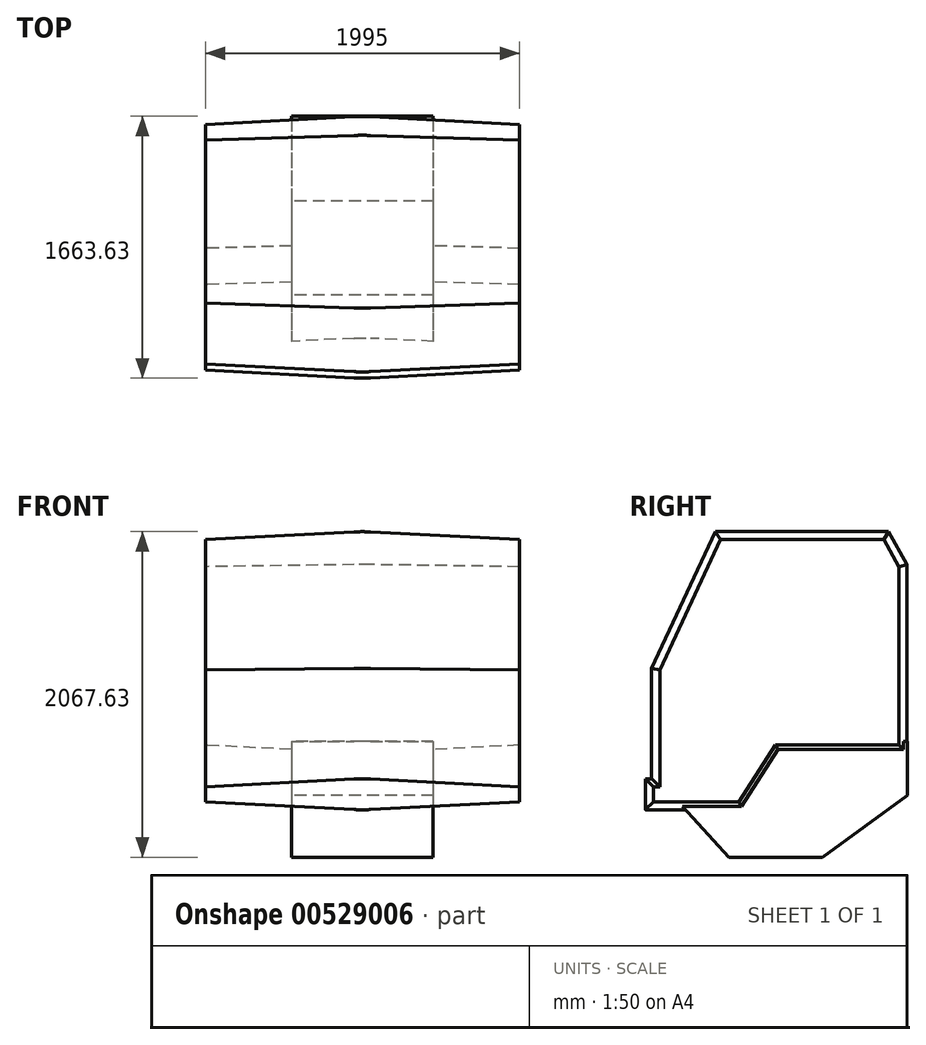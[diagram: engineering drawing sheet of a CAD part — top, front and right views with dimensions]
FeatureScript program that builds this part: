
annotation { "Feature Type Name" : "Feature", "Feature Type Description" : "" }
export const myFeature = defineFeature(function(context is Context, id is Id, definition is map)
    precondition{}
    {
        {
            var Q0;
            Q0=qCreatedBy(makeId("Right.planeOp"),FACE);
            var sketch = newSketch(context, id + "F0", { "sketchPlane" : qUnion([Q0])});
            skLineSegment(sketch, "E0", {"start": v(0, 0) * mm, "end": v(0, 2408.1) * mm, "construction": true});
            skLineSegment(sketch, "E1", {"start": v(540, 660) * mm, "end": v(540, 1859) * mm});
            skLineSegment(sketch, "E2", {"start": v(540, 1859) * mm, "end": v(420, 2069) * mm});
            skLineSegment(sketch, "E3", {"start": v(420, 2069) * mm, "end": v(-679.78, 2069) * mm});
            skLineSegment(sketch, "E4", {"start": v(-679.78, 2069) * mm, "end": v(-1085, 1200) * mm});
            skLineSegment(sketch, "E5", {"start": v(-1085, 1200) * mm, "end": v(-1085, 500) * mm});
            skLineSegment(sketch, "E6", {"start": v(-1085, 500) * mm, "end": v(-1125, 500) * mm});
            skLineSegment(sketch, "E7", {"start": v(-1125, 500) * mm, "end": v(-1125, 300) * mm});
            skLineSegment(sketch, "E8", {"start": v(-1125, 300) * mm, "end": v(-500, 300) * mm});
            skLineSegment(sketch, "E9", {"start": v(-500, 300) * mm, "end": v(-270, 660) * mm});
            skLineSegment(sketch, "E10", {"start": v(-270, 660) * mm, "end": v(540, 660) * mm});
            skLineSegment(sketch, "E11", {"start": v(0, 560) * mm, "end": v(1375.56, 560) * mm, "construction": true});
            skSolve(sketch);
        }
        {
            var Q0;
            Q0=makeQuery(id+"F0.imprint","IMPRINT",FACE,{"disambiguationData":[TD([[makeQuery(id+"F0.imprint","IMPRINT",EDGE,{"derivedFrom":sQuery(id+"F0.wireOp",EDGE,"E1")}),1.0]])]});
            extrude(context, id + "F1", {"entities" : qUnion([Q0]), "endBound" : BoundingType.SYMMETRIC, "depth" : 1995 * mm, "offsetDistance" : 25 * mm, "hasDraft" : true, "draftAngle" : 3 * degree, "draftPullDirection" : true});
        }
        {
            var Q0;
            Q0=qCreatedBy(makeId("Right.planeOp"),FACE);
            var sketch = newSketch(context, id + "F2", { "sketchPlane" : qUnion([Q0])});
            skLineSegment(sketch, "E12.0", {"start": v(-270, 660) * mm, "end": v(540, 660) * mm, "construction": true});
            skLineSegment(sketch, "E13", {"start": v(540, 660) * mm, "end": v(540, 391.7) * mm});
            skLineSegment(sketch, "E14", {"start": v(540, 391.7) * mm, "end": v(0, 0) * mm});
            skLineSegment(sketch, "E15", {"start": v(0, 0) * mm, "end": v(-594.52, 0) * mm});
            skLineSegment(sketch, "E16", {"start": v(-594.52, 735.26) * mm, "end": v(540, 735.26) * mm});
            skLineSegment(sketch, "E17", {"start": v(540, 735.26) * mm, "end": v(540, 660) * mm});
            skLineSegment(sketch, "E18", {"start": v(-594.52, 0) * mm, "end": v(-956.76, 397.83) * mm});
            skLineSegment(sketch, "E19", {"start": v(-956.76, 397.83) * mm, "end": v(-594.52, 735.26) * mm});
            skSolve(sketch);
        }
        {
            var Q0;
            Q0=makeQuery(id+"F2.imprint","IMPRINT",FACE,{"disambiguationData":[TD([[makeQuery(id+"F2.imprint","IMPRINT",EDGE,{"derivedFrom":sQuery(id+"F2.wireOp",EDGE,"E13")}),-1.0]])]});
            extrude(context, id + "F3", {"entities" : qUnion([Q0]), "operationType" : NewBodyOperationType.ADD, "endBound" : BoundingType.SYMMETRIC, "depth" : 900 * mm, "offsetDistance" : 25 * mm});
        }
        {
            var Q0;
            {var subQ0=makeQuery(id+"F1.opExtrude","SWEPT_FACE",FACE,{"disambiguationData":[OSD([sQuery(id+"F0.wireOp",EDGE,"E7")])]});Q0=makeQuery(id+"F1.*.booleanUnion.opBoolean","MERGE",EDGE,{"derivedFrom":[makeQuery(id+"F1.*.split.splitOp","SPLIT_SURFACE_INTERSECT",EDGE,{"derivedFrom":[subQ0]}),makeQuery(id+"F1.*.split.splitOp","SPLIT_SURFACE_INTERSECT",EDGE,{"derivedFrom":[subQ0],"isFromBackBody":true})]});}
            var Q1;
            {var subQ0=makeQuery(id+"F1.opExtrude","SWEPT_FACE",FACE,{"disambiguationData":[OSD([sQuery(id+"F0.wireOp",EDGE,"E6")])]});Q1=makeQuery(id+"F1.*.booleanUnion.opBoolean","MERGE",EDGE,{"derivedFrom":[makeQuery(id+"F1.*.split.splitOp","SPLIT_SURFACE_INTERSECT",EDGE,{"derivedFrom":[subQ0]}),makeQuery(id+"F1.*.split.splitOp","SPLIT_SURFACE_INTERSECT",EDGE,{"derivedFrom":[subQ0],"isFromBackBody":true})]});}
            var Q2;
            {var subQ0=makeQuery(id+"F1.opExtrude","SWEPT_FACE",FACE,{"disambiguationData":[OSD([sQuery(id+"F0.wireOp",EDGE,"E5")])]});Q2=makeQuery(id+"F1.*.booleanUnion.opBoolean","MERGE",EDGE,{"derivedFrom":[makeQuery(id+"F1.*.split.splitOp","SPLIT_SURFACE_INTERSECT",EDGE,{"derivedFrom":[subQ0]}),makeQuery(id+"F1.*.split.splitOp","SPLIT_SURFACE_INTERSECT",EDGE,{"derivedFrom":[subQ0],"isFromBackBody":true})]});}
            var Q3;
            {var subQ0=makeQuery(id+"F1.opExtrude","SWEPT_FACE",FACE,{"disambiguationData":[OSD([sQuery(id+"F0.wireOp",EDGE,"E4")])]});Q3=makeQuery(id+"F1.*.booleanUnion.opBoolean","MERGE",EDGE,{"derivedFrom":[makeQuery(id+"F1.*.split.splitOp","SPLIT_SURFACE_INTERSECT",EDGE,{"derivedFrom":[subQ0]}),makeQuery(id+"F1.*.split.splitOp","SPLIT_SURFACE_INTERSECT",EDGE,{"derivedFrom":[subQ0],"isFromBackBody":true})]});}
            var Q4;
            {var subQ0=makeQuery(id+"F1.opExtrude","SWEPT_FACE",FACE,{"disambiguationData":[OSD([sQuery(id+"F0.wireOp",EDGE,"E3")])]});Q4=makeQuery(id+"F1.*.booleanUnion.opBoolean","MERGE",EDGE,{"derivedFrom":[makeQuery(id+"F1.*.split.splitOp","SPLIT_SURFACE_INTERSECT",EDGE,{"derivedFrom":[subQ0]}),makeQuery(id+"F1.*.split.splitOp","SPLIT_SURFACE_INTERSECT",EDGE,{"derivedFrom":[subQ0],"isFromBackBody":true})]});}
            var Q5;
            {var subQ0=makeQuery(id+"F1.opExtrude","SWEPT_FACE",FACE,{"disambiguationData":[OSD([sQuery(id+"F0.wireOp",EDGE,"E2")])]});Q5=makeQuery(id+"F1.*.booleanUnion.opBoolean","MERGE",EDGE,{"derivedFrom":[makeQuery(id+"F1.*.split.splitOp","SPLIT_SURFACE_INTERSECT",EDGE,{"derivedFrom":[subQ0]}),makeQuery(id+"F1.*.split.splitOp","SPLIT_SURFACE_INTERSECT",EDGE,{"derivedFrom":[subQ0],"isFromBackBody":true})]});}
            var Q6;
            {var subQ0=makeQuery(id+"F1.opExtrude","SWEPT_FACE",FACE,{"disambiguationData":[OSD([sQuery(id+"F0.wireOp",EDGE,"E1")])]});Q6=makeQuery(id+"F1.*.booleanUnion.opBoolean","MERGE",EDGE,{"derivedFrom":[makeQuery(id+"F1.*.split.splitOp","SPLIT_SURFACE_INTERSECT",EDGE,{"derivedFrom":[subQ0]}),makeQuery(id+"F1.*.split.splitOp","SPLIT_SURFACE_INTERSECT",EDGE,{"derivedFrom":[subQ0],"isFromBackBody":true})]});}
            var Q7;
            {var subQ0=makeQuery(id+"F1.opExtrude","SWEPT_FACE",FACE,{"disambiguationData":[OSD([sQuery(id+"F0.wireOp",EDGE,"E10")])]});Q7=makeQuery(id+"F1.*.booleanUnion.opBoolean","MERGE",EDGE,{"derivedFrom":[makeQuery(id+"F1.*.split.splitOp","SPLIT_SURFACE_INTERSECT",EDGE,{"derivedFrom":[subQ0]}),makeQuery(id+"F1.*.split.splitOp","SPLIT_SURFACE_INTERSECT",EDGE,{"derivedFrom":[subQ0],"isFromBackBody":true})]});}
            var Q8;
            {var subQ0=makeQuery(id+"F1.opExtrude","SWEPT_FACE",FACE,{"disambiguationData":[OSD([sQuery(id+"F0.wireOp",EDGE,"E9")])]});Q8=makeQuery(id+"F1.*.booleanUnion.opBoolean","MERGE",EDGE,{"derivedFrom":[makeQuery(id+"F1.*.split.splitOp","SPLIT_SURFACE_INTERSECT",EDGE,{"derivedFrom":[subQ0]}),makeQuery(id+"F1.*.split.splitOp","SPLIT_SURFACE_INTERSECT",EDGE,{"derivedFrom":[subQ0],"isFromBackBody":true})]});}
            var Q9;
            {var subQ0=makeQuery(id+"F1.opExtrude","SWEPT_FACE",FACE,{"disambiguationData":[OSD([sQuery(id+"F0.wireOp",EDGE,"E8")])]});Q9=makeQuery(id+"F1.*.booleanUnion.opBoolean","MERGE",EDGE,{"derivedFrom":[makeQuery(id+"F1.*.split.splitOp","SPLIT_SURFACE_INTERSECT",EDGE,{"derivedFrom":[subQ0]}),makeQuery(id+"F1.*.split.splitOp","SPLIT_SURFACE_INTERSECT",EDGE,{"derivedFrom":[subQ0],"isFromBackBody":true})]});}
            fillet(context, id + "F4", {"entities" : qUnion([Q0, Q1, Q2, Q3, Q4, Q5, Q6, Q7, Q8, Q9]), "radius" : 1000 * mm, "tangentPropagation" : true, "allowEdgeOverflow" : false});
        }
    });
